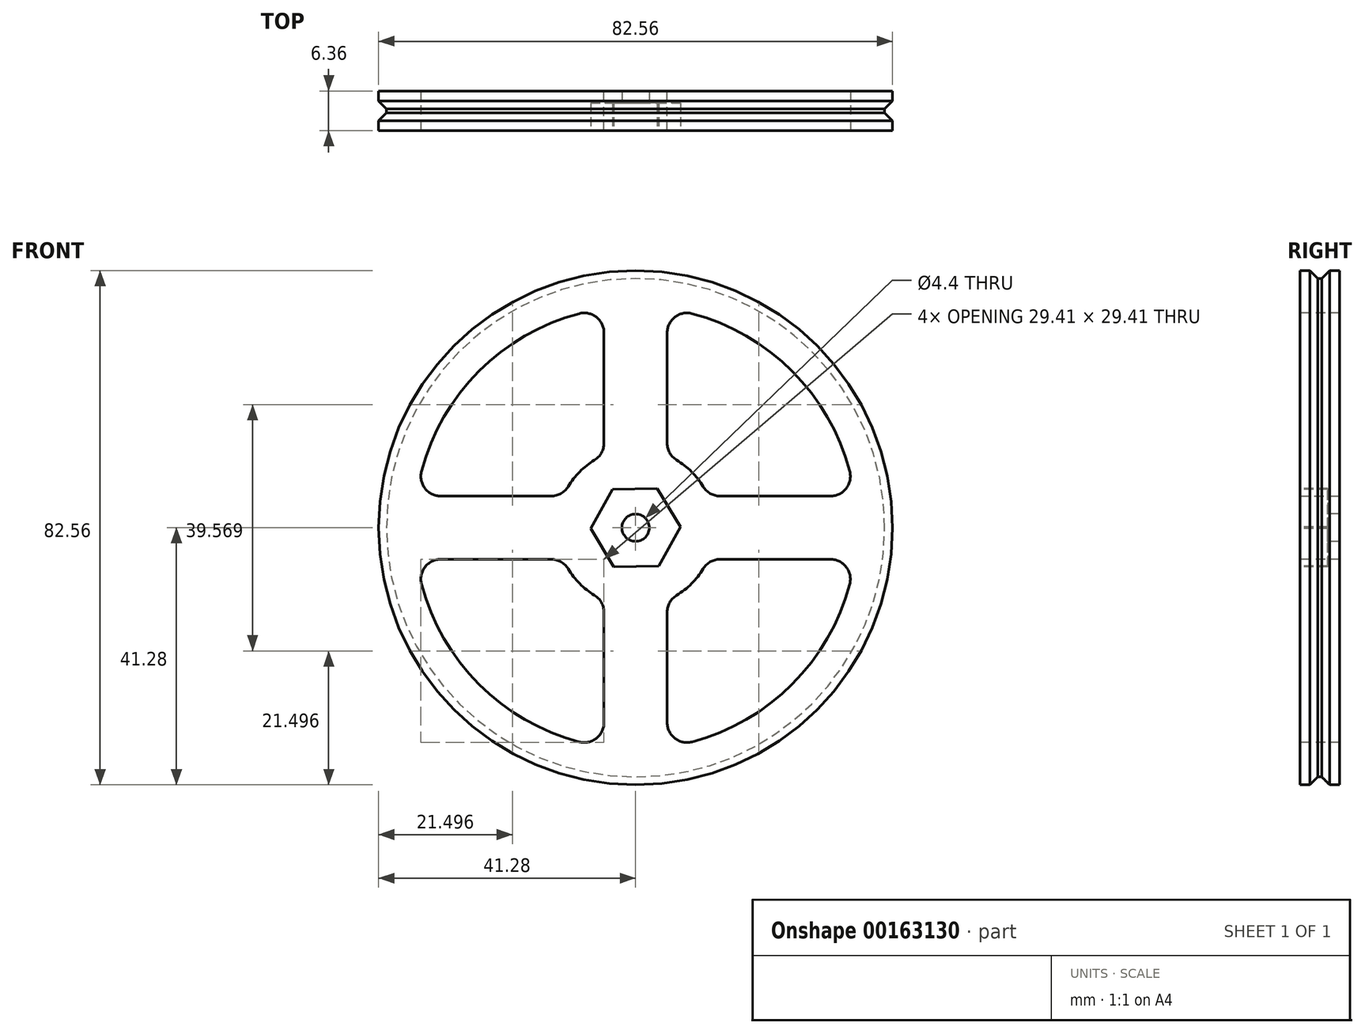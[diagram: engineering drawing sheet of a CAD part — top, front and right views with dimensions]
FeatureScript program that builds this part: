
annotation { "Feature Type Name" : "Feature", "Feature Type Description" : "" }
export const myFeature = defineFeature(function(context is Context, id is Id, definition is map)
    precondition{}
    {
        {
            var Q0;
            Q0=qCreatedBy(makeId("Front.planeOp"),FACE);
            var sketch = newSketch(context, id + "F0", { "sketchPlane" : qUnion([Q0])});
            skCircle(sketch, "E0", {"center": v(0, 0) * mm, "radius": 40 * mm});
            skCircle(sketch, "E1.0", {"center": v(0, 0) * mm, "radius": 41.28 * mm});
            skCircle(sketch, "E2.cCircle", {"center": v(0, 0) * mm, "radius": 6.35 * mm, "construction": true});
            skLineSegment(sketch, "E2.0", {"start": v(-3.67, 6.35) * mm, "end": v(3.67, 6.35) * mm});
            skLineSegment(sketch, "E2.1", {"start": v(3.67, 6.35) * mm, "end": v(7.33, 0) * mm});
            skLineSegment(sketch, "E2.2", {"start": v(7.33, 0) * mm, "end": v(3.67, -6.35) * mm});
            skLineSegment(sketch, "E2.3", {"start": v(3.67, -6.35) * mm, "end": v(-3.67, -6.35) * mm});
            skLineSegment(sketch, "E2.4", {"start": v(-3.67, -6.35) * mm, "end": v(-7.33, 0) * mm});
            skLineSegment(sketch, "E2.5", {"start": v(-7.33, 0) * mm, "end": v(-3.67, 6.35) * mm});
            skPoint(sketch, "E2.0.midPoint", {"position": v(0, 6.35) * mm});
            skSolve(sketch);
        }
        {
            var Q0;
            Q0=makeQuery(id+"F0.imprint","IMPRINT",FACE,{"disambiguationData":[TD([[makeQuery(id+"F0.imprint","IMPRINT",EDGE,{"derivedFrom":sQuery(id+"F0.wireOp",EDGE,"E0")}),1.0]])]});
            var Q1;
            Q1=makeQuery(id+"F0.imprint","IMPRINT",FACE,{"disambiguationData":[TD([[makeQuery(id+"F0.imprint","IMPRINT",EDGE,{"derivedFrom":sQuery(id+"F0.wireOp",EDGE,"E0")}),-1.0]])]});
            var Q2;
            Q2=makeQuery(id+"F0.imprint","IMPRINT",FACE,{"disambiguationData":[TD([[makeQuery(id+"F0.imprint","IMPRINT",EDGE,{"derivedFrom":sQuery(id+"F0.wireOp",EDGE,"E2.0")}),-1.0]])]});
            extrude(context, id + "F1", {"entities" : qUnion([Q0, Q1, Q2]), "endBound" : BoundingType.SYMMETRIC, "depth" : 6.35 * mm});
        }
        {
            var Q0;
            Q0=makeQuery(id+"F1.opExtrude","CAP_FACE",FACE,{"disambiguationData":[OSD([sQuery(id+"F0.wireOp",EDGE,"E1.0")])],"isStart":false});
            var sketch = newSketch(context, id + "F2", { "sketchPlane" : qUnion([Q0])});
            skCircle(sketch, "E3.cCircle", {"center": v(0, 0) * mm, "radius": 6.22 * mm, "construction": true});
            skLineSegment(sketch, "E3.0", {"start": v(3.49, 6.28) * mm, "end": v(7.18, 0.12) * mm});
            skLineSegment(sketch, "E3.1", {"start": v(7.18, 0.12) * mm, "end": v(3.7, -6.16) * mm});
            skLineSegment(sketch, "E3.2", {"start": v(3.7, -6.16) * mm, "end": v(-3.49, -6.28) * mm});
            skLineSegment(sketch, "E3.3", {"start": v(-3.49, -6.28) * mm, "end": v(-7.18, -0.12) * mm});
            skLineSegment(sketch, "E3.4", {"start": v(-7.18, -0.12) * mm, "end": v(-3.7, 6.16) * mm});
            skLineSegment(sketch, "E3.5", {"start": v(-3.7, 6.16) * mm, "end": v(3.49, 6.28) * mm});
            skPoint(sketch, "E3.0.midPoint", {"position": v(5.34, 3.2) * mm});
            skSolve(sketch);
        }
        {
            var Q0;
            Q0=qSketchRegion(id+"F2",true);
            extrude(context, id + "F3", {"entities" : qUnion([Q0]), "operationType" : NewBodyOperationType.REMOVE, "oppositeDirection" : true, "depth" : 4.44 * mm});
        }
        {
            var Q0;
            Q0=makeQuery(id+"F1.opExtrude","CAP_FACE",FACE,{"disambiguationData":[OSD([sQuery(id+"F0.wireOp",EDGE,"E1.0"),sQuery(id+"F0.wireOp",EDGE,"E2.0"),sQuery(id+"F0.wireOp",EDGE,"E2.1"),sQuery(id+"F0.wireOp",EDGE,"E2.2"),sQuery(id+"F0.wireOp",EDGE,"E2.3"),sQuery(id+"F0.wireOp",EDGE,"E2.4"),sQuery(id+"F0.wireOp",EDGE,"E2.5")])],"isStart":false});
            var sketch = newSketch(context, id + "F4", { "sketchPlane" : qUnion([Q0])});
            skCircle(sketch, "E4", {"center": v(0, 0) * mm, "radius": 35.56 * mm});
            skCircle(sketch, "E5.0", {"center": v(0, 0) * mm, "radius": 12.7 * mm});
            skLineSegment(sketch, "E6", {"start": v(0, -12.7) * mm, "end": v(0, -35.56) * mm});
            skLineSegment(sketch, "E7.0", {"start": v(-5.08, -11.64) * mm, "end": v(-5.08, -35.2) * mm});
            skLineSegment(sketch, "E8.0", {"start": v(5.08, -11.64) * mm, "end": v(5.08, -35.2) * mm});
            skLineSegment(sketch, "E9.1.0", {"start": v(11.64, -5.08) * mm, "end": v(35.2, -5.08) * mm});
            skLineSegment(sketch, "E9.1.1", {"start": v(11.64, 5.08) * mm, "end": v(35.2, 5.08) * mm});
            skLineSegment(sketch, "E9.2.0", {"start": v(5.08, 11.64) * mm, "end": v(5.08, 35.2) * mm});
            skLineSegment(sketch, "E9.2.1", {"start": v(-5.08, 11.64) * mm, "end": v(-5.08, 35.2) * mm});
            skLineSegment(sketch, "E9.3.0", {"start": v(-11.64, 5.08) * mm, "end": v(-35.2, 5.08) * mm});
            skLineSegment(sketch, "E9.3.1", {"start": v(-11.64, -5.08) * mm, "end": v(-35.2, -5.08) * mm});
            skSolve(sketch);
        }
        {
            var Q0;
            {var subQ0=sQuery(id+"F4.wireOp",EDGE,"E7.0");Q0=makeQuery(id+"F4.imprint","IMPRINT",FACE,{"disambiguationData":[TD([[makeQuery(id+"F4.imprint","IMPRINT",EDGE,{"derivedFrom":subQ0}),-1.0]])]});}
            var Q1;
            {var subQ0=sQuery(id+"F4.wireOp",EDGE,"E9.2.1");Q1=makeQuery(id+"F4.imprint","IMPRINT",FACE,{"disambiguationData":[TD([[makeQuery(id+"F4.imprint","IMPRINT",EDGE,{"derivedFrom":subQ0}),1.0]])]});}
            var Q2;
            {var subQ0=sQuery(id+"F4.wireOp",EDGE,"E9.1.1");Q2=makeQuery(id+"F4.imprint","IMPRINT",FACE,{"disambiguationData":[TD([[makeQuery(id+"F4.imprint","IMPRINT",EDGE,{"derivedFrom":subQ0}),1.0]])]});}
            var Q3;
            {var subQ0=sQuery(id+"F4.wireOp",EDGE,"E8.0");Q3=makeQuery(id+"F4.imprint","IMPRINT",FACE,{"disambiguationData":[TD([[makeQuery(id+"F4.imprint","IMPRINT",EDGE,{"derivedFrom":subQ0}),1.0]])]});}
            extrude(context, id + "F5", {"entities" : qUnion([Q0, Q1, Q2, Q3]), "operationType" : NewBodyOperationType.REMOVE, "endBound" : BoundingType.THROUGH_ALL, "oppositeDirection" : true, "depth" : 25.4 * mm});
        }
        {
            var Q0;
            Q0=makeQuery(id+"F5.boolean.opBoolean","COPY",EDGE,{"derivedFrom":makeQuery(id+"F5.opExtrude","SWEPT_EDGE",EDGE,{"disambiguationData":[OSD([sQuery(id+"F4.wireOp",EDGE,"E4"),sQuery(id+"F4.wireOp",EDGE,"27957d35-a56d-4cfa-9457-b1a0cf56e145.3.0")])]})});
            var Q1;
            Q1=makeQuery(id+"F5.boolean.opBoolean","COPY",EDGE,{"derivedFrom":makeQuery(id+"F5.opExtrude","SWEPT_EDGE",EDGE,{"disambiguationData":[OSD([sQuery(id+"F4.wireOp",EDGE,"E4"),sQuery(id+"F4.wireOp",EDGE,"e348a229-b992-494f-8d39-545bbdace99f.0")])]})});
            var Q2;
            Q2=makeQuery(id+"F5.boolean.opBoolean","COPY",EDGE,{"derivedFrom":makeQuery(id+"F5.opExtrude","SWEPT_EDGE",EDGE,{"disambiguationData":[OSD([sQuery(id+"F4.wireOp",EDGE,"E5.0"),sQuery(id+"F4.wireOp",EDGE,"27957d35-a56d-4cfa-9457-b1a0cf56e145.1.1")])]})});
            var Q3;
            Q3=makeQuery(id+"F5.boolean.opBoolean","COPY",EDGE,{"derivedFrom":makeQuery(id+"F5.opExtrude","SWEPT_EDGE",EDGE,{"disambiguationData":[OSD([sQuery(id+"F4.wireOp",EDGE,"E5.0"),sQuery(id+"F4.wireOp",EDGE,"27957d35-a56d-4cfa-9457-b1a0cf56e145.2.0")])]})});
            var Q4;
            Q4=makeQuery(id+"F5.boolean.opBoolean","COPY",EDGE,{"derivedFrom":makeQuery(id+"F5.opExtrude","SWEPT_EDGE",EDGE,{"disambiguationData":[OSD([sQuery(id+"F4.wireOp",EDGE,"E4"),sQuery(id+"F4.wireOp",EDGE,"27957d35-a56d-4cfa-9457-b1a0cf56e145.2.1")])]})});
            var Q5;
            Q5=makeQuery(id+"F5.boolean.opBoolean","COPY",EDGE,{"derivedFrom":makeQuery(id+"F5.opExtrude","SWEPT_EDGE",EDGE,{"disambiguationData":[OSD([sQuery(id+"F4.wireOp",EDGE,"E5.0"),sQuery(id+"F4.wireOp",EDGE,"27957d35-a56d-4cfa-9457-b1a0cf56e145.2.1")])]})});
            var Q6;
            Q6=makeQuery(id+"F5.boolean.opBoolean","COPY",EDGE,{"derivedFrom":makeQuery(id+"F5.opExtrude","SWEPT_EDGE",EDGE,{"disambiguationData":[OSD([sQuery(id+"F4.wireOp",EDGE,"E4"),sQuery(id+"F4.wireOp",EDGE,"27957d35-a56d-4cfa-9457-b1a0cf56e145.2.0")])]})});
            var Q7;
            Q7=makeQuery(id+"F5.boolean.opBoolean","COPY",EDGE,{"derivedFrom":makeQuery(id+"F5.opExtrude","SWEPT_EDGE",EDGE,{"disambiguationData":[OSD([sQuery(id+"F4.wireOp",EDGE,"E4"),sQuery(id+"F4.wireOp",EDGE,"27957d35-a56d-4cfa-9457-b1a0cf56e145.1.1")])]})});
            var Q8;
            Q8=makeQuery(id+"F5.boolean.opBoolean","COPY",EDGE,{"derivedFrom":makeQuery(id+"F5.opExtrude","SWEPT_EDGE",EDGE,{"disambiguationData":[OSD([sQuery(id+"F4.wireOp",EDGE,"E4"),sQuery(id+"F4.wireOp",EDGE,"27957d35-a56d-4cfa-9457-b1a0cf56e145.1.0")])]})});
            var Q9;
            Q9=makeQuery(id+"F5.boolean.opBoolean","COPY",EDGE,{"derivedFrom":makeQuery(id+"F5.opExtrude","SWEPT_EDGE",EDGE,{"disambiguationData":[OSD([sQuery(id+"F4.wireOp",EDGE,"E5.0"),sQuery(id+"F4.wireOp",EDGE,"27957d35-a56d-4cfa-9457-b1a0cf56e145.3.1")])]})});
            var Q10;
            Q10=makeQuery(id+"F5.boolean.opBoolean","COPY",EDGE,{"derivedFrom":makeQuery(id+"F5.opExtrude","SWEPT_EDGE",EDGE,{"disambiguationData":[OSD([sQuery(id+"F4.wireOp",EDGE,"E5.0"),sQuery(id+"F4.wireOp",EDGE,"0dbcb386-fed9-4ae0-a355-918e704f70ac.0")])]})});
            var Q11;
            Q11=makeQuery(id+"F5.boolean.opBoolean","COPY",EDGE,{"derivedFrom":makeQuery(id+"F5.opExtrude","SWEPT_EDGE",EDGE,{"disambiguationData":[OSD([sQuery(id+"F4.wireOp",EDGE,"E4"),sQuery(id+"F4.wireOp",EDGE,"0dbcb386-fed9-4ae0-a355-918e704f70ac.0")])]})});
            var Q12;
            Q12=makeQuery(id+"F5.boolean.opBoolean","COPY",EDGE,{"derivedFrom":makeQuery(id+"F5.opExtrude","SWEPT_EDGE",EDGE,{"disambiguationData":[OSD([sQuery(id+"F4.wireOp",EDGE,"E4"),sQuery(id+"F4.wireOp",EDGE,"27957d35-a56d-4cfa-9457-b1a0cf56e145.3.1")])]})});
            var Q13;
            Q13=makeQuery(id+"F5.boolean.opBoolean","COPY",EDGE,{"derivedFrom":makeQuery(id+"F5.opExtrude","SWEPT_EDGE",EDGE,{"disambiguationData":[OSD([sQuery(id+"F4.wireOp",EDGE,"E5.0"),sQuery(id+"F4.wireOp",EDGE,"27957d35-a56d-4cfa-9457-b1a0cf56e145.3.0")])]})});
            var Q14;
            Q14=makeQuery(id+"F5.boolean.opBoolean","COPY",EDGE,{"derivedFrom":makeQuery(id+"F5.opExtrude","SWEPT_EDGE",EDGE,{"disambiguationData":[OSD([sQuery(id+"F4.wireOp",EDGE,"E5.0"),sQuery(id+"F4.wireOp",EDGE,"e348a229-b992-494f-8d39-545bbdace99f.0")])]})});
            var Q15;
            Q15=makeQuery(id+"F5.boolean.opBoolean","COPY",EDGE,{"derivedFrom":makeQuery(id+"F5.opExtrude","SWEPT_EDGE",EDGE,{"disambiguationData":[OSD([sQuery(id+"F4.wireOp",EDGE,"E5.0"),sQuery(id+"F4.wireOp",EDGE,"27957d35-a56d-4cfa-9457-b1a0cf56e145.1.0")])]})});
            fillet(context, id + "F6", {"entities" : qUnion([Q0, Q1, Q2, Q3, Q4, Q5, Q6, Q7, Q8, Q9, Q10, Q11, Q12, Q13, Q14, Q15]), "radius" : 3.17 * mm, "tangentPropagation" : true, "allowEdgeOverflow" : false});
        }
        {
            var Q0;
            Q0=makeQuery(id+"F3.boolean.opBoolean","COPY",FACE,{"derivedFrom":makeQuery(id+"F3.opExtrude","CAP_FACE",FACE,{"disambiguationData":[OSD([sQuery(id+"F2.wireOp",EDGE,"E3.0"),sQuery(id+"F2.wireOp",EDGE,"E3.1"),sQuery(id+"F2.wireOp",EDGE,"E3.2"),sQuery(id+"F2.wireOp",EDGE,"E3.3"),sQuery(id+"F2.wireOp",EDGE,"E3.4"),sQuery(id+"F2.wireOp",EDGE,"E3.5")])],"isStart":false})});
            var sketch = newSketch(context, id + "F7", { "sketchPlane" : qUnion([Q0])});
            skPoint(sketch, "E10", {"position": v(0, 0) * mm});
            skSolve(sketch);
        }
        {
            var Q0;
            Q0=sQuery(id+"F7.wireOp",VERTEX,"E10");
            var Q1;
            Q1=makeQuery(id+"F1.opExtrude","SWEPT_BODY",BODY,{"disambiguationData":[OSD([sQuery(id+"F0.wireOp",EDGE,"E1.0")])]});
            hole(context, id + "F8", {"style" : HoleStyle.SIMPLE, "endStyle" : HoleEndStyle.THROUGH, "standardTappedOrClearance" : lookupTablePath({ "standard" : "ISO", "fit" : "Normal", "size" : "M4", "type" : "Clearance" }), "standardBlindInLast" : lookupTablePath({ "fit" : "Standard", "standard" : "ISO", "size" : "M4", "type" : "Clearance" }), "holeDiameter" : 4.4 * mm, "locations" : qUnion([Q0]), "scope" : qUnion([Q1]), "isTappedThrough" : true});
        }
        {
            var Q0;
            Q0=qCreatedBy(makeId("Front.planeOp"),FACE);
            var sketch = newSketch(context, id + "F9", { "sketchPlane" : qUnion([Q0])});
            skCircle(sketch, "E11", {"center": v(0, 0) * mm, "radius": 40 * mm});
            skCircle(sketch, "E12.0", {"center": v(0, 0) * mm, "radius": 41.28 * mm});
            skSolve(sketch);
        }
        {
            var Q0;
            Q0=qSketchRegion(id+"F9",true);
            extrude(context, id + "F10", {"entities" : qUnion([Q0]), "operationType" : NewBodyOperationType.REMOVE, "endBound" : BoundingType.SYMMETRIC, "oppositeDirection" : true, "depth" : 3.17 * mm});
        }
        {
            var Q0;
            Q0=makeQuery(id+"F10.boolean.opBoolean","COPY",EDGE,{"derivedFrom":makeQuery(id+"F10.opExtrude","CAP_EDGE",EDGE,{"disambiguationData":[OSD([sQuery(id+"F9.wireOp",EDGE,"E11")])],"isStart":false})});
            var Q1;
            Q1=makeQuery(id+"F10.boolean.opBoolean","COPY",EDGE,{"derivedFrom":makeQuery(id+"F10.opExtrude","CAP_EDGE",EDGE,{"disambiguationData":[OSD([sQuery(id+"F9.wireOp",EDGE,"E11")])],"isStart":true})});
            chamfer(context, id + "F11", {"entities" : qUnion([Q0, Q1]), "width" : 1.27 * mm, "tangentPropagation" : true});
        }
    });
